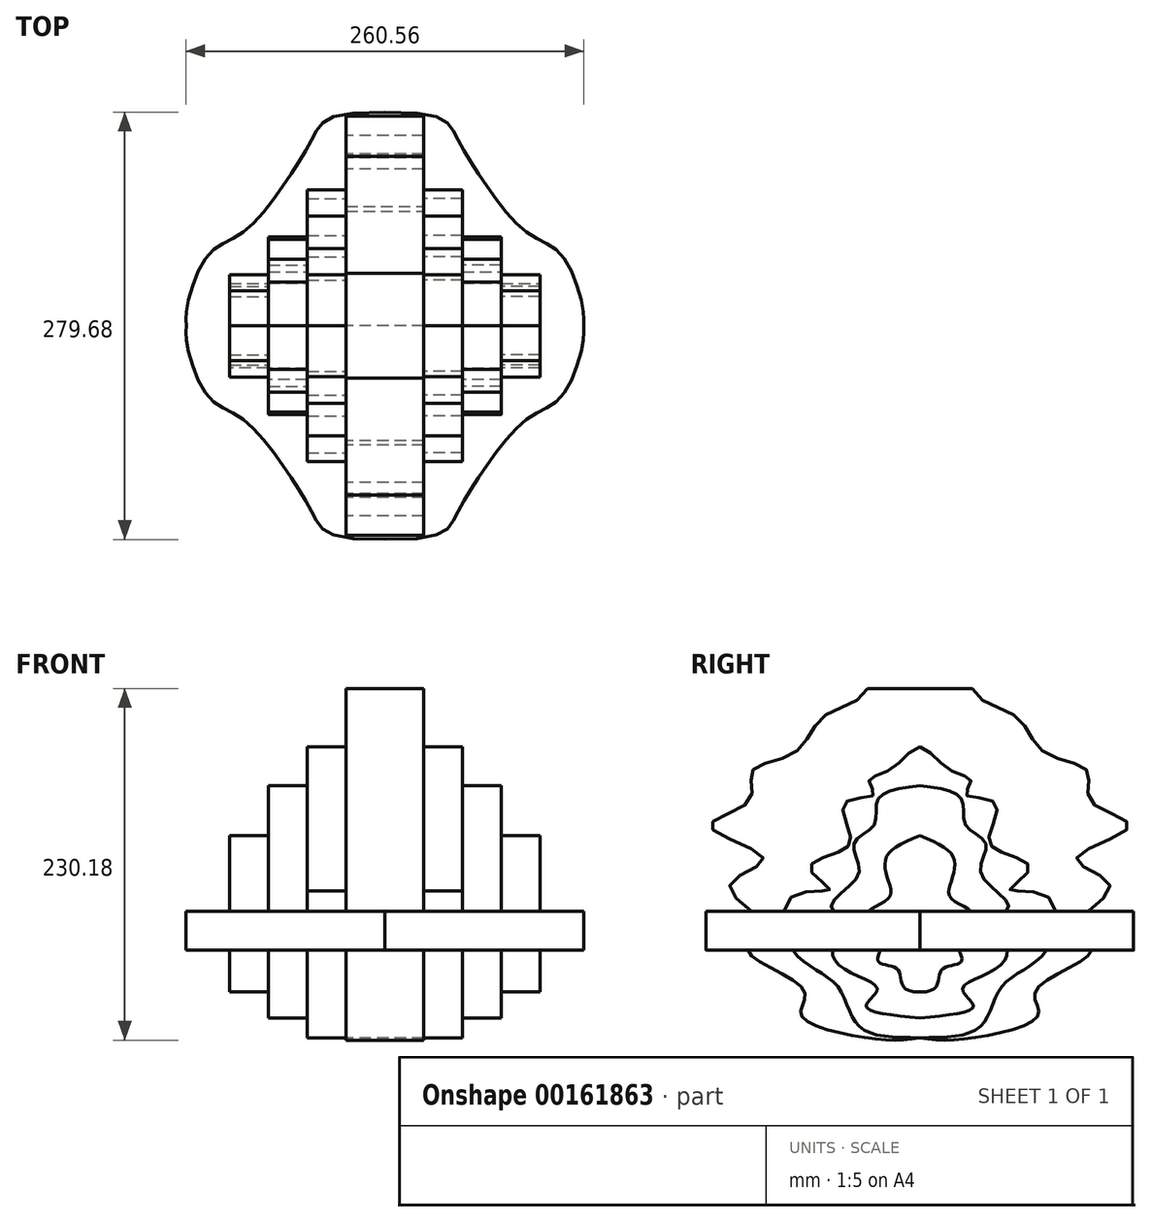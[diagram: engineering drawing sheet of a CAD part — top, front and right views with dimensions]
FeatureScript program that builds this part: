
annotation { "Feature Type Name" : "Feature", "Feature Type Description" : "" }
export const myFeature = defineFeature(function(context is Context, id is Id, definition is map)
    precondition{}
    {
        {
            var Q0;
            Q0=qCreatedBy(makeId("Right.planeOp"),FACE);
            var sketch = newSketch(context, id + "F0", { "sketchPlane" : qUnion([Q0])});
            skFitSpline(sketch, "E0", {"points": [v(0, -57.32) * mm, v(-35.01, -57.32) * mm, v(-77.83, -41.83) * mm, v(-75.8, -26.58) * mm, v(-112.48, 0) * mm, v(-102.92, 15.6) * mm, v(-124.4, 42.37) * mm, v(-102.5, 59.72) * mm, v(-137.06, 81.02) * mm, v(-111.58, 97.68) * mm, v(-109.99, 116.9) * mm, v(-81.65, 129.37) * mm, v(-63.14, 152.84) * mm, v(-34.32, 171.28) * mm], "startDerivative": vector(-373.15, -75.56) * mm, "endDerivative": vector(147.92, 391.95) * mm});
            skLineSegment(sketch, "E1", {"start": v(-34.32, 171.28) * mm, "end": v(0, 171.28) * mm});
            skLineSegment(sketch, "E2", {"start": v(0, 171.28) * mm, "end": v(0, -57.32) * mm});
            skSolve(sketch);
        }
        {
            var Q0;
            Q0 = qSketchRegion(id + "F0", true);
            extrude(context, id + "F1", {"entities" : qUnion([Q0]), "depth" : 25.4 * mm});
        }
        {
            var Q0;
            Q0=makeQuery(id+"F1.opExtrude","CAP_FACE",FACE,{"disambiguationData":[OSD([sQuery(id+"F0.wireOp",EDGE,"E0"),sQuery(id+"F0.wireOp",EDGE,"E1"),sQuery(id+"F0.wireOp",EDGE,"E2")])],"isStart":false});
            var sketch = newSketch(context, id + "F2", { "sketchPlane" : qUnion([Q0])});
            skFitSpline(sketch, "E3", {"points": [v(0, -57.32) * mm, v(-40.24, -49.4) * mm, v(-54.2, -23.2) * mm, v(-83.07, 0) * mm, v(-82.68, 35.75) * mm, v(-59.06, 39.59) * mm, v(-71.9, 53.35) * mm, v(-53.23, 64.26) * mm, v(-45.32, 74.13) * mm, v(-49.4, 96.4) * mm, v(-30.07, 101.84) * mm, v(-33.43, 110.59) * mm, v(-19.49, 118.03) * mm, v(0, 133.18) * mm], "startDerivative": vector(-510.14, 4.26) * mm, "endDerivative": vector(278.59, 76.1) * mm});
            skLineSegment(sketch, "E4", {"start": v(0, 133.18) * mm, "end": v(0, -57.32) * mm});
            skSolve(sketch);
        }
        {
            var Q0;
            Q0 = qSketchRegion(id + "F2", true);
            extrude(context, id + "F3", {"entities" : qUnion([Q0]), "operationType" : NewBodyOperationType.ADD, "depth" : 25.4 * mm});
        }
        {
            var Q0;
            Q0=makeQuery(id+"F3.opExtrude","CAP_FACE",FACE,{"disambiguationData":[OSD([sQuery(id+"F2.wireOp",EDGE,"E3"),sQuery(id+"F2.wireOp",EDGE,"E4")])],"isStart":false});
            var sketch = newSketch(context, id + "F4", { "sketchPlane" : qUnion([Q0])});
            skFitSpline(sketch, "E5", {"points": [v(0, -44.26) * mm, v(-35.12, -36.13) * mm, v(-27.89, -25.38) * mm, v(-53.5, -9.2) * mm, v(-52.08, 7.75) * mm, v(-31.8, 13.96) * mm, v(-57.83, 27.36) * mm, v(-40.25, 49.58) * mm, v(-43.3, 69.27) * mm, v(-29.99, 81.94) * mm, v(-27.42, 98.6) * mm, v(0, 107.82) * mm], "startDerivative": vector(-472.75, 41.01) * mm, "endDerivative": vector(356.52, 47.09) * mm});
            skLineSegment(sketch, "E6", {"start": v(0, 107.82) * mm, "end": v(0, -44.26) * mm});
            skSolve(sketch);
        }
        {
            var Q0;
            Q0 = qSketchRegion(id + "F4", true);
            extrude(context, id + "F5", {"entities" : qUnion([Q0]), "operationType" : NewBodyOperationType.ADD, "depth" : 25.4 * mm});
        }
        {
            var Q0;
            Q0=makeQuery(id+"F5.opExtrude","CAP_FACE",FACE,{"disambiguationData":[OSD([sQuery(id+"F4.wireOp",EDGE,"E5"),sQuery(id+"F4.wireOp",EDGE,"E6")])],"isStart":false});
            var sketch = newSketch(context, id + "F6", { "sketchPlane" : qUnion([Q0])});
            skFitSpline(sketch, "E7", {"points": [v(0, -27.34) * mm, v(-14.11, -12.97) * mm, v(-27.35, -7.2) * mm, v(-22.97, 10.78) * mm, v(-34.14, 23.99) * mm, v(-20.73, 33.6) * mm, v(-20.43, 44.8) * mm, v(-22.26, 60.07) * mm, v(0, 74.83) * mm], "startDerivative": vector(-348.86, -11.71) * mm, "endDerivative": vector(235.12, 92.42) * mm});
            skLineSegment(sketch, "E8", {"start": v(0, 74.83) * mm, "end": v(0, -27.34) * mm});
            skSolve(sketch);
        }
        {
            var Q0;
            Q0 = qSketchRegion(id + "F6", true);
            extrude(context, id + "F7", {"entities" : qUnion([Q0]), "operationType" : NewBodyOperationType.ADD, "depth" : 25.4 * mm});
        }
        {
            var Q0;
            Q0=qCreatedBy(makeId("Top.planeOp"),FACE);
            var sketch = newSketch(context, id + "F8", { "sketchPlane" : qUnion([Q0])});
            skFitSpline(sketch, "E9", {"points": [v(0, -139.8) * mm, v(47.08, -123.05) * mm, v(65.81, -92.91) * mm, v(94.14, -60.2) * mm, v(115.42, -46.5) * mm, v(129.74, -10.76) * mm, v(130.01, 0) * mm], "startDerivative": vector(588.35, -9.6) * mm, "endDerivative": vector(-8.3, 89.06) * mm});
            skLineSegment(sketch, "E10", {"start": v(0, -139.8) * mm, "end": v(0, 0) * mm});
            skLineSegment(sketch, "E11", {"start": v(0, 0) * mm, "end": v(130.01, 0) * mm});
            skSolve(sketch);
        }
        {
            var Q0;
            Q0 = qSketchRegion(id + "F8", true);
            extrude(context, id + "F9", {"entities" : qUnion([Q0]), "operationType" : NewBodyOperationType.ADD, "depth" : 25.4 * mm});
        }
        {
            var Q0;
            Q0=makeQuery(id+"F1.opExtrude","SWEPT_BODY",BODY,{"disambiguationData":[OSD([sQuery(id+"F0.wireOp",EDGE,"E0"),sQuery(id+"F0.wireOp",EDGE,"E1"),sQuery(id+"F0.wireOp",EDGE,"E2")])]});
            var Q1;
            Q1=makeQuery(id+"F9.boolean.opBoolean","MERGE",FACE,{"derivedFrom":[makeQuery(id+"F7.boolean.opBoolean","MERGE",FACE,{"derivedFrom":[makeQuery(id+"F5.boolean.opBoolean","MERGE",FACE,{"derivedFrom":[makeQuery(id+"F3.boolean.opBoolean","MERGE",FACE,{"derivedFrom":[makeQuery(id+"F1.opExtrude","SWEPT_FACE",FACE,{"disambiguationData":[OSD([sQuery(id+"F0.wireOp",EDGE,"E2")])]}),makeQuery(id+"F3.opExtrude","SWEPT_FACE",FACE,{"disambiguationData":[OSD([sQuery(id+"F2.wireOp",EDGE,"E4")])]})]}),makeQuery(id+"F5.opExtrude","SWEPT_FACE",FACE,{"disambiguationData":[OSD([sQuery(id+"F4.wireOp",EDGE,"E6")])]})]}),makeQuery(id+"F7.opExtrude","SWEPT_FACE",FACE,{"disambiguationData":[OSD([sQuery(id+"F6.wireOp",EDGE,"E8")])]})]}),makeQuery(id+"F9.opExtrude","SWEPT_FACE",FACE,{"disambiguationData":[OSD([sQuery(id+"F8.wireOp",EDGE,"E11")])]})]});
            mirror(context, id + "F10", {"operationType" : NewBodyOperationType.ADD, "entities" : qUnion([Q0]), "mirrorPlane" : qUnion([Q1])});
        }
        {
            var Q0;
            Q0=makeQuery(id+"F1.opExtrude","SWEPT_BODY",BODY,{"disambiguationData":[OSD([sQuery(id+"F0.wireOp",EDGE,"E0"),sQuery(id+"F0.wireOp",EDGE,"E1"),sQuery(id+"F0.wireOp",EDGE,"E2")])]});
            var Q1;
            {var subQ0=makeQuery(id+"F9.boolean.opBoolean","MERGE",FACE,{"derivedFrom":[makeQuery(id+"F1.opExtrude","CAP_FACE",FACE,{"disambiguationData":[OSD([sQuery(id+"F0.wireOp",EDGE,"E0"),sQuery(id+"F0.wireOp",EDGE,"E1"),sQuery(id+"F0.wireOp",EDGE,"E2")])],"isStart":true}),makeQuery(id+"F9.opExtrude","SWEPT_FACE",FACE,{"disambiguationData":[OSD([sQuery(id+"F8.wireOp",EDGE,"E10")])]})]});Q1=makeQuery(id+"F10.boolean.opBoolean","MERGE",FACE,{"derivedFrom":[subQ0,makeQuery(id+"F10.opPattern","COPY",FACE,{"derivedFrom":subQ0,"instanceName":"1"})]});}
            mirror(context, id + "F11", {"operationType" : NewBodyOperationType.ADD, "entities" : qUnion([Q0]), "mirrorPlane" : qUnion([Q1])});
        }
    });
